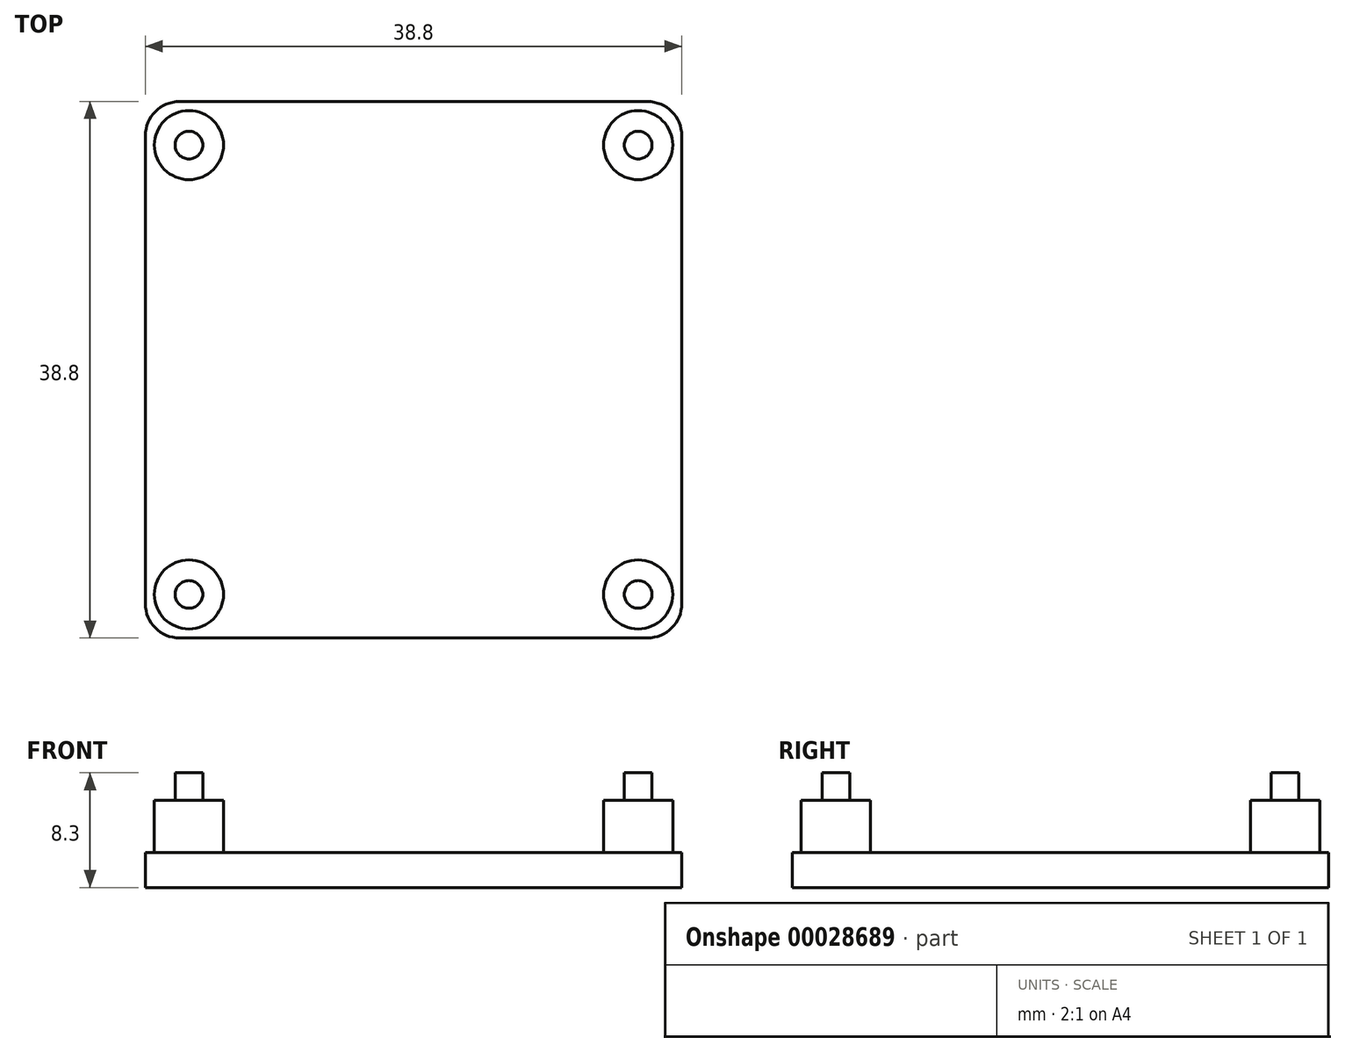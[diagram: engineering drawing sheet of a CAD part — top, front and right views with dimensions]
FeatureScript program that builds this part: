
annotation { "Feature Type Name" : "Feature", "Feature Type Description" : "" }
export const myFeature = defineFeature(function(context is Context, id is Id, definition is map)
    precondition{}
    {
        {
            var Q0;
            Q0=qCreatedBy(makeId("Top.planeOp"),FACE);
            var sketch = newSketch(context, id + "F0", { "sketchPlane" : qUnion([Q0])});
            skLineSegment(sketch, "E0.bottom", {"start": v(-16.25, -16.25) * mm, "end": v(16.25, -16.25) * mm});
            skLineSegment(sketch, "E0.top", {"start": v(-16.25, 16.25) * mm, "end": v(16.25, 16.25) * mm});
            skLineSegment(sketch, "E0.left", {"start": v(-16.25, -16.25) * mm, "end": v(-16.25, 16.25) * mm});
            skLineSegment(sketch, "E0.right", {"start": v(16.25, -16.25) * mm, "end": v(16.25, 16.25) * mm});
            skCircle(sketch, "E1", {"center": v(-16.25, 16.25) * mm, "radius": 2.5 * mm});
            skCircle(sketch, "E2", {"center": v(16.25, 16.25) * mm, "radius": 2.5 * mm});
            skCircle(sketch, "E3", {"center": v(16.25, -16.25) * mm, "radius": 2.5 * mm});
            skCircle(sketch, "E4", {"center": v(-16.25, -16.25) * mm, "radius": 2.5 * mm});
            skLineSegment(sketch, "E5", {"start": v(0, 16.25) * mm, "end": v(0, -16.25) * mm});
            skLineSegment(sketch, "E6", {"start": v(-16.25, 0) * mm, "end": v(16.25, 0) * mm});
            skLineSegment(sketch, "E7.bottom", {"start": v(-19.4, 19.4) * mm, "end": v(19.4, 19.4) * mm});
            skLineSegment(sketch, "E7.top", {"start": v(-19.4, -19.4) * mm, "end": v(19.4, -19.4) * mm});
            skLineSegment(sketch, "E7.left", {"start": v(-19.4, 19.4) * mm, "end": v(-19.4, -19.4) * mm});
            skLineSegment(sketch, "E7.right", {"start": v(19.4, 19.4) * mm, "end": v(19.4, -19.4) * mm});
            skLineSegment(sketch, "E8", {"start": v(-16.25, 0) * mm, "end": v(-19.4, 0) * mm});
            skLineSegment(sketch, "E9", {"start": v(16.25, 0) * mm, "end": v(19.4, 0) * mm});
            skLineSegment(sketch, "E10", {"start": v(0, 16.25) * mm, "end": v(0, 19.4) * mm});
            skLineSegment(sketch, "E11", {"start": v(0, -16.25) * mm, "end": v(0, -19.4) * mm});
            skSolve(sketch);
        }
        {
            var Q0;
            {var subQ1=sQuery(id+"F0.wireOp",EDGE,"E9");Q0=makeQuery(id+"F0.imprint","IMPRINT",FACE,{"disambiguationData":[TD([[makeQuery(id+"F0.imprint","IMPRINT",EDGE,{"derivedFrom":subQ1}),1.0]])]});}
            var Q1;
            {var subQ3=sQuery(id+"F0.wireOp",EDGE,"E0.top");var subQ7=sQuery(id+"F0.wireOp",EDGE,"E2");var subQ9=makeQuery(id+"F0.imprint","INTERSECT",VERTEX,{"derivedFrom":[subQ3,subQ7]});Q1=makeQuery(id+"F0.imprint","IMPRINT",FACE,{"disambiguationData":[TD([[makeQuery(id+"F0.imprint","IMPRINT",EDGE,{"disambiguationData":[TD([[subQ9,-1.0]])],"derivedFrom":subQ7}),-1.0]])]});}
            var Q2;
            {var subQ5=sQuery(id+"F0.wireOp",EDGE,"E0.top");var subQ7=sQuery(id+"F0.wireOp",EDGE,"E1");var subQ9=makeQuery(id+"F0.imprint","INTERSECT",VERTEX,{"derivedFrom":[subQ5,subQ7]});Q2=makeQuery(id+"F0.imprint","IMPRINT",FACE,{"disambiguationData":[TD([[makeQuery(id+"F0.imprint","IMPRINT",EDGE,{"disambiguationData":[TD([[subQ9,1.0]])],"derivedFrom":subQ7}),-1.0]])]});}
            var Q3;
            {var subQ5=sQuery(id+"F0.wireOp",EDGE,"E0.bottom");var subQ7=sQuery(id+"F0.wireOp",EDGE,"E4");var subQ9=makeQuery(id+"F0.imprint","INTERSECT",VERTEX,{"derivedFrom":[subQ5,subQ7]});Q3=makeQuery(id+"F0.imprint","IMPRINT",FACE,{"disambiguationData":[TD([[makeQuery(id+"F0.imprint","IMPRINT",EDGE,{"disambiguationData":[TD([[subQ9,-1.0]])],"derivedFrom":subQ7}),-1.0]])]});}
            var Q4;
            {var subQ5=sQuery(id+"F0.wireOp",EDGE,"E0.bottom");var subQ7=sQuery(id+"F0.wireOp",EDGE,"E3");var subQ9=makeQuery(id+"F0.imprint","INTERSECT",VERTEX,{"derivedFrom":[subQ5,subQ7]});Q4=makeQuery(id+"F0.imprint","IMPRINT",FACE,{"disambiguationData":[TD([[makeQuery(id+"F0.imprint","IMPRINT",EDGE,{"disambiguationData":[TD([[subQ9,1.0]])],"derivedFrom":subQ7}),-1.0]])]});}
            var Q5;
            {var subQ1=sQuery(id+"F0.wireOp",EDGE,"E9");Q5=makeQuery(id+"F0.imprint","IMPRINT",FACE,{"disambiguationData":[TD([[makeQuery(id+"F0.imprint","IMPRINT",EDGE,{"derivedFrom":subQ1}),-1.0]])]});}
            var Q6;
            {var subQ1=sQuery(id+"F0.wireOp",EDGE,"E8");Q6=makeQuery(id+"F0.imprint","IMPRINT",FACE,{"disambiguationData":[TD([[makeQuery(id+"F0.imprint","IMPRINT",EDGE,{"derivedFrom":subQ1}),1.0]])]});}
            var Q7;
            {var subQ1=sQuery(id+"F0.wireOp",EDGE,"E8");Q7=makeQuery(id+"F0.imprint","IMPRINT",FACE,{"disambiguationData":[TD([[makeQuery(id+"F0.imprint","IMPRINT",EDGE,{"derivedFrom":subQ1}),-1.0]])]});}
            var Q8;
            {var subQ1=sQuery(id+"F0.wireOp",EDGE,"E0.right");var subQ3=sQuery(id+"F0.wireOp",EDGE,"E0.top");var subQ5=makeQuery(id+"F0.imprint","INTERSECT",VERTEX,{"derivedFrom":[subQ3,subQ1]});Q8=makeQuery(id+"F0.imprint","IMPRINT",FACE,{"disambiguationData":[TD([[makeQuery(id+"F0.imprint","IMPRINT",EDGE,{"disambiguationData":[TD([[subQ5,1.0]])],"derivedFrom":subQ3}),1.0]])]});}
            var Q9;
            {var subQ1=sQuery(id+"F0.wireOp",EDGE,"E0.right");var subQ3=sQuery(id+"F0.wireOp",EDGE,"E0.top");var subQ5=makeQuery(id+"F0.imprint","INTERSECT",VERTEX,{"derivedFrom":[subQ3,subQ1]});Q9=makeQuery(id+"F0.imprint","IMPRINT",FACE,{"disambiguationData":[TD([[makeQuery(id+"F0.imprint","IMPRINT",EDGE,{"disambiguationData":[TD([[subQ5,1.0]])],"derivedFrom":subQ3}),-1.0]])]});}
            var Q10;
            {var subQ1=sQuery(id+"F0.wireOp",EDGE,"E0.left");var subQ3=sQuery(id+"F0.wireOp",EDGE,"E0.top");var subQ5=makeQuery(id+"F0.imprint","INTERSECT",VERTEX,{"derivedFrom":[subQ3,subQ1]});Q10=makeQuery(id+"F0.imprint","IMPRINT",FACE,{"disambiguationData":[TD([[makeQuery(id+"F0.imprint","IMPRINT",EDGE,{"disambiguationData":[TD([[subQ5,-1.0]])],"derivedFrom":subQ3}),-1.0]])]});}
            var Q11;
            {var subQ1=sQuery(id+"F0.wireOp",EDGE,"E0.left");var subQ3=sQuery(id+"F0.wireOp",EDGE,"E0.top");var subQ5=makeQuery(id+"F0.imprint","INTERSECT",VERTEX,{"derivedFrom":[subQ3,subQ1]});Q11=makeQuery(id+"F0.imprint","IMPRINT",FACE,{"disambiguationData":[TD([[makeQuery(id+"F0.imprint","IMPRINT",EDGE,{"disambiguationData":[TD([[subQ5,-1.0]])],"derivedFrom":subQ3}),1.0]])]});}
            var Q12;
            {var subQ1=sQuery(id+"F0.wireOp",EDGE,"E0.left");var subQ3=sQuery(id+"F0.wireOp",EDGE,"E0.bottom");var subQ5=makeQuery(id+"F0.imprint","INTERSECT",VERTEX,{"derivedFrom":[subQ3,subQ1]});Q12=makeQuery(id+"F0.imprint","IMPRINT",FACE,{"disambiguationData":[TD([[makeQuery(id+"F0.imprint","IMPRINT",EDGE,{"disambiguationData":[TD([[subQ5,-1.0]])],"derivedFrom":subQ3}),-1.0]])]});}
            var Q13;
            {var subQ1=sQuery(id+"F0.wireOp",EDGE,"E0.left");var subQ3=sQuery(id+"F0.wireOp",EDGE,"E0.bottom");var subQ5=makeQuery(id+"F0.imprint","INTERSECT",VERTEX,{"derivedFrom":[subQ3,subQ1]});Q13=makeQuery(id+"F0.imprint","IMPRINT",FACE,{"disambiguationData":[TD([[makeQuery(id+"F0.imprint","IMPRINT",EDGE,{"disambiguationData":[TD([[subQ5,-1.0]])],"derivedFrom":subQ3}),1.0]])]});}
            var Q14;
            {var subQ1=sQuery(id+"F0.wireOp",EDGE,"E0.right");var subQ3=sQuery(id+"F0.wireOp",EDGE,"E0.bottom");var subQ5=makeQuery(id+"F0.imprint","INTERSECT",VERTEX,{"derivedFrom":[subQ3,subQ1]});Q14=makeQuery(id+"F0.imprint","IMPRINT",FACE,{"disambiguationData":[TD([[makeQuery(id+"F0.imprint","IMPRINT",EDGE,{"disambiguationData":[TD([[subQ5,1.0]])],"derivedFrom":subQ3}),-1.0]])]});}
            var Q15;
            {var subQ1=sQuery(id+"F0.wireOp",EDGE,"E0.right");var subQ3=sQuery(id+"F0.wireOp",EDGE,"E0.bottom");var subQ5=makeQuery(id+"F0.imprint","INTERSECT",VERTEX,{"derivedFrom":[subQ3,subQ1]});Q15=makeQuery(id+"F0.imprint","IMPRINT",FACE,{"disambiguationData":[TD([[makeQuery(id+"F0.imprint","IMPRINT",EDGE,{"disambiguationData":[TD([[subQ5,1.0]])],"derivedFrom":subQ3}),1.0]])]});}
            extrude(context, id + "F1", {"entities" : qUnion([Q0, Q1, Q2, Q3, Q4, Q5, Q6, Q7, Q8, Q9, Q10, Q11, Q12, Q13, Q14, Q15]), "depth" : 2.54 * mm});
        }
        {
            var Q0;
            {var subQ1=sQuery(id+"F0.wireOp",EDGE,"E0.left");var subQ3=sQuery(id+"F0.wireOp",EDGE,"E0.bottom");var subQ5=makeQuery(id+"F0.imprint","INTERSECT",VERTEX,{"derivedFrom":[subQ3,subQ1]});Q0=makeQuery(id+"F0.imprint","IMPRINT",FACE,{"disambiguationData":[TD([[makeQuery(id+"F0.imprint","IMPRINT",EDGE,{"disambiguationData":[TD([[subQ5,-1.0]])],"derivedFrom":subQ3}),1.0]])]});}
            var Q1;
            {var subQ1=sQuery(id+"F0.wireOp",EDGE,"E0.left");var subQ3=sQuery(id+"F0.wireOp",EDGE,"E0.bottom");var subQ5=makeQuery(id+"F0.imprint","INTERSECT",VERTEX,{"derivedFrom":[subQ3,subQ1]});Q1=makeQuery(id+"F0.imprint","IMPRINT",FACE,{"disambiguationData":[TD([[makeQuery(id+"F0.imprint","IMPRINT",EDGE,{"disambiguationData":[TD([[subQ5,-1.0]])],"derivedFrom":subQ3}),-1.0]])]});}
            var Q2;
            {var subQ1=sQuery(id+"F0.wireOp",EDGE,"E0.right");var subQ3=sQuery(id+"F0.wireOp",EDGE,"E0.bottom");var subQ5=makeQuery(id+"F0.imprint","INTERSECT",VERTEX,{"derivedFrom":[subQ3,subQ1]});Q2=makeQuery(id+"F0.imprint","IMPRINT",FACE,{"disambiguationData":[TD([[makeQuery(id+"F0.imprint","IMPRINT",EDGE,{"disambiguationData":[TD([[subQ5,1.0]])],"derivedFrom":subQ3}),-1.0]])]});}
            var Q3;
            {var subQ1=sQuery(id+"F0.wireOp",EDGE,"E0.right");var subQ3=sQuery(id+"F0.wireOp",EDGE,"E0.bottom");var subQ5=makeQuery(id+"F0.imprint","INTERSECT",VERTEX,{"derivedFrom":[subQ3,subQ1]});Q3=makeQuery(id+"F0.imprint","IMPRINT",FACE,{"disambiguationData":[TD([[makeQuery(id+"F0.imprint","IMPRINT",EDGE,{"disambiguationData":[TD([[subQ5,1.0]])],"derivedFrom":subQ3}),1.0]])]});}
            var Q4;
            {var subQ1=sQuery(id+"F0.wireOp",EDGE,"E0.right");var subQ3=sQuery(id+"F0.wireOp",EDGE,"E0.top");var subQ5=makeQuery(id+"F0.imprint","INTERSECT",VERTEX,{"derivedFrom":[subQ3,subQ1]});Q4=makeQuery(id+"F0.imprint","IMPRINT",FACE,{"disambiguationData":[TD([[makeQuery(id+"F0.imprint","IMPRINT",EDGE,{"disambiguationData":[TD([[subQ5,1.0]])],"derivedFrom":subQ3}),1.0]])]});}
            var Q5;
            {var subQ1=sQuery(id+"F0.wireOp",EDGE,"E0.right");var subQ3=sQuery(id+"F0.wireOp",EDGE,"E0.top");var subQ5=makeQuery(id+"F0.imprint","INTERSECT",VERTEX,{"derivedFrom":[subQ3,subQ1]});Q5=makeQuery(id+"F0.imprint","IMPRINT",FACE,{"disambiguationData":[TD([[makeQuery(id+"F0.imprint","IMPRINT",EDGE,{"disambiguationData":[TD([[subQ5,1.0]])],"derivedFrom":subQ3}),-1.0]])]});}
            var Q6;
            {var subQ1=sQuery(id+"F0.wireOp",EDGE,"E0.left");var subQ3=sQuery(id+"F0.wireOp",EDGE,"E0.top");var subQ5=makeQuery(id+"F0.imprint","INTERSECT",VERTEX,{"derivedFrom":[subQ3,subQ1]});Q6=makeQuery(id+"F0.imprint","IMPRINT",FACE,{"disambiguationData":[TD([[makeQuery(id+"F0.imprint","IMPRINT",EDGE,{"disambiguationData":[TD([[subQ5,-1.0]])],"derivedFrom":subQ3}),-1.0]])]});}
            var Q7;
            {var subQ1=sQuery(id+"F0.wireOp",EDGE,"E0.left");var subQ3=sQuery(id+"F0.wireOp",EDGE,"E0.top");var subQ5=makeQuery(id+"F0.imprint","INTERSECT",VERTEX,{"derivedFrom":[subQ3,subQ1]});Q7=makeQuery(id+"F0.imprint","IMPRINT",FACE,{"disambiguationData":[TD([[makeQuery(id+"F0.imprint","IMPRINT",EDGE,{"disambiguationData":[TD([[subQ5,-1.0]])],"derivedFrom":subQ3}),1.0]])]});}
            extrude(context, id + "F2", {"entities" : qUnion([Q0, Q1, Q2, Q3, Q4, Q5, Q6, Q7]), "operationType" : NewBodyOperationType.ADD, "depth" : 6.3 * mm});
        }
        {
            var Q0;
            Q0=makeQuery(id+"F2.opExtrude","CAP_FACE",FACE,{"disambiguationData":[OSD([sQuery(id+"F0.wireOp",EDGE,"E3")])],"isStart":false});
            var sketch = newSketch(context, id + "F3", { "sketchPlane" : qUnion([Q0])});
            skCircle(sketch, "E12", {"center": v(-16.25, 16.25) * mm, "radius": 1 * mm});
            skCircle(sketch, "E13", {"center": v(16.25, 16.25) * mm, "radius": 1 * mm});
            skCircle(sketch, "E14", {"center": v(16.25, -16.25) * mm, "radius": 1 * mm});
            skCircle(sketch, "E15", {"center": v(-16.25, -16.25) * mm, "radius": 1 * mm});
            skSolve(sketch);
        }
        {
            var Q0;
            Q0=makeQuery(id+"F3.imprint","IMPRINT",FACE,{"disambiguationData":[TD([[makeQuery(id+"F3.imprint","IMPRINT",EDGE,{"derivedFrom":sQuery(id+"F3.wireOp",EDGE,"E12")}),1.0]])]});
            var Q1;
            Q1=makeQuery(id+"F3.imprint","IMPRINT",FACE,{"disambiguationData":[TD([[makeQuery(id+"F3.imprint","IMPRINT",EDGE,{"derivedFrom":sQuery(id+"F3.wireOp",EDGE,"E13")}),1.0]])]});
            var Q2;
            Q2=makeQuery(id+"F3.imprint","IMPRINT",FACE,{"disambiguationData":[TD([[makeQuery(id+"F3.imprint","IMPRINT",EDGE,{"derivedFrom":sQuery(id+"F3.wireOp",EDGE,"E14")}),1.0]])]});
            var Q3;
            Q3=makeQuery(id+"F3.imprint","IMPRINT",FACE,{"disambiguationData":[TD([[makeQuery(id+"F3.imprint","IMPRINT",EDGE,{"derivedFrom":sQuery(id+"F3.wireOp",EDGE,"E15")}),1.0]])]});
            extrude(context, id + "F4", {"entities" : qUnion([Q0, Q1, Q2, Q3]), "operationType" : NewBodyOperationType.ADD, "depth" : 2 * mm});
        }
        {
            var Q0;
            Q0=makeQuery(id+"F1.opExtrude","SWEPT_EDGE",EDGE,{"disambiguationData":[OSD([sQuery(id+"F0.wireOp",EDGE,"E7.top"),sQuery(id+"F0.wireOp",EDGE,"E7.left")])]});
            var Q1;
            Q1=makeQuery(id+"F1.opExtrude","SWEPT_EDGE",EDGE,{"disambiguationData":[OSD([sQuery(id+"F0.wireOp",EDGE,"E7.top"),sQuery(id+"F0.wireOp",EDGE,"E7.right")])]});
            var Q2;
            Q2=makeQuery(id+"F1.opExtrude","SWEPT_EDGE",EDGE,{"disambiguationData":[OSD([sQuery(id+"F0.wireOp",EDGE,"E7.bottom"),sQuery(id+"F0.wireOp",EDGE,"E7.right")])]});
            var Q3;
            Q3=makeQuery(id+"F1.opExtrude","SWEPT_EDGE",EDGE,{"disambiguationData":[OSD([sQuery(id+"F0.wireOp",EDGE,"E7.bottom"),sQuery(id+"F0.wireOp",EDGE,"E7.left")])]});
            fillet(context, id + "F5", {"entities" : qUnion([Q0, Q1, Q2, Q3]), "radius" : 2.46 * mm, "tangentPropagation" : true, "allowEdgeOverflow" : false});
        }
    });
